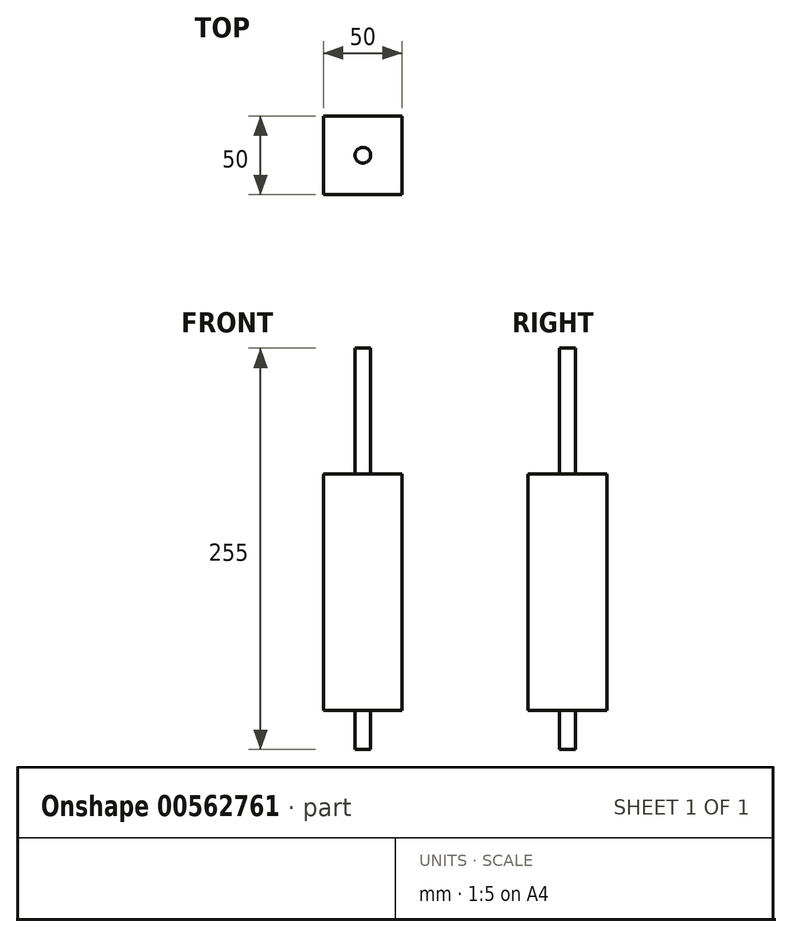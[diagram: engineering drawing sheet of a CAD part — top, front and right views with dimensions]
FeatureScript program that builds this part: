
annotation { "Feature Type Name" : "Feature", "Feature Type Description" : "" }
export const myFeature = defineFeature(function(context is Context, id is Id, definition is map)
    precondition{}
    {
        {
            var Q0;
            Q0=qCreatedBy(makeId("Top.planeOp"),FACE);
            var sketch = newSketch(context, id + "F0", { "sketchPlane" : qUnion([Q0])});
            skLineSegment(sketch, "E0.bottom", {"start": v(25, 25) * mm, "end": v(-25, 25) * mm});
            skLineSegment(sketch, "E0.top", {"start": v(25, -25) * mm, "end": v(-25, -25) * mm});
            skLineSegment(sketch, "E0.left", {"start": v(25, 25) * mm, "end": v(25, -25) * mm});
            skLineSegment(sketch, "E0.right", {"start": v(-25, 25) * mm, "end": v(-25, -25) * mm});
            skPoint(sketch, "E0.middle", {"position": v(0, 0) * mm});
            skSolve(sketch);
        }
        {
            var Q0;
            Q0=makeQuery(id+"F0.imprint","IMPRINT",FACE,{"disambiguationData":[TD([[makeQuery(id+"F0.imprint","IMPRINT",EDGE,{"derivedFrom":sQuery(id+"F0.wireOp",EDGE,"E0.bottom")}),1.0]])]});
            extrude(context, id + "F1", {"entities" : qUnion([Q0]), "endBound" : BoundingType.SYMMETRIC, "depth" : 150 * mm, "offsetDistance" : 25 * mm});
        }
        {
            var Q0;
            Q0=makeQuery(id+"F1.opExtrude","CAP_FACE",FACE,{"disambiguationData":[OSD([sQuery(id+"F0.wireOp",EDGE,"E0.bottom"),sQuery(id+"F0.wireOp",EDGE,"E0.top"),sQuery(id+"F0.wireOp",EDGE,"E0.left"),sQuery(id+"F0.wireOp",EDGE,"E0.right")])],"isStart":false});
            var sketch = newSketch(context, id + "F2", { "sketchPlane" : qUnion([Q0])});
            skCircle(sketch, "E1", {"center": v(0, 0) * mm, "radius": 5 * mm});
            skSolve(sketch);
        }
        {
            var Q0;
            Q0=qSketchRegion(id+"F2",true);
            extrude(context, id + "F3", {"entities" : qUnion([Q0]), "operationType" : NewBodyOperationType.ADD, "depth" : 80 * mm, "offsetDistance" : 25 * mm});
        }
        {
            var Q0;
            Q0=makeQuery(id+"F1.opExtrude","CAP_FACE",FACE,{"disambiguationData":[OSD([sQuery(id+"F0.wireOp",EDGE,"E0.bottom"),sQuery(id+"F0.wireOp",EDGE,"E0.top"),sQuery(id+"F0.wireOp",EDGE,"E0.left"),sQuery(id+"F0.wireOp",EDGE,"E0.right")])],"isStart":true});
            var sketch = newSketch(context, id + "F4", { "sketchPlane" : qUnion([Q0])});
            skCircle(sketch, "E2", {"center": v(0, 0) * mm, "radius": 5 * mm});
            skSolve(sketch);
        }
        {
            var Q0;
            Q0=qSketchRegion(id+"F4",true);
            extrude(context, id + "F5", {"entities" : qUnion([Q0]), "operationType" : NewBodyOperationType.ADD, "depth" : 25 * mm, "offsetDistance" : 25 * mm});
        }
    });
